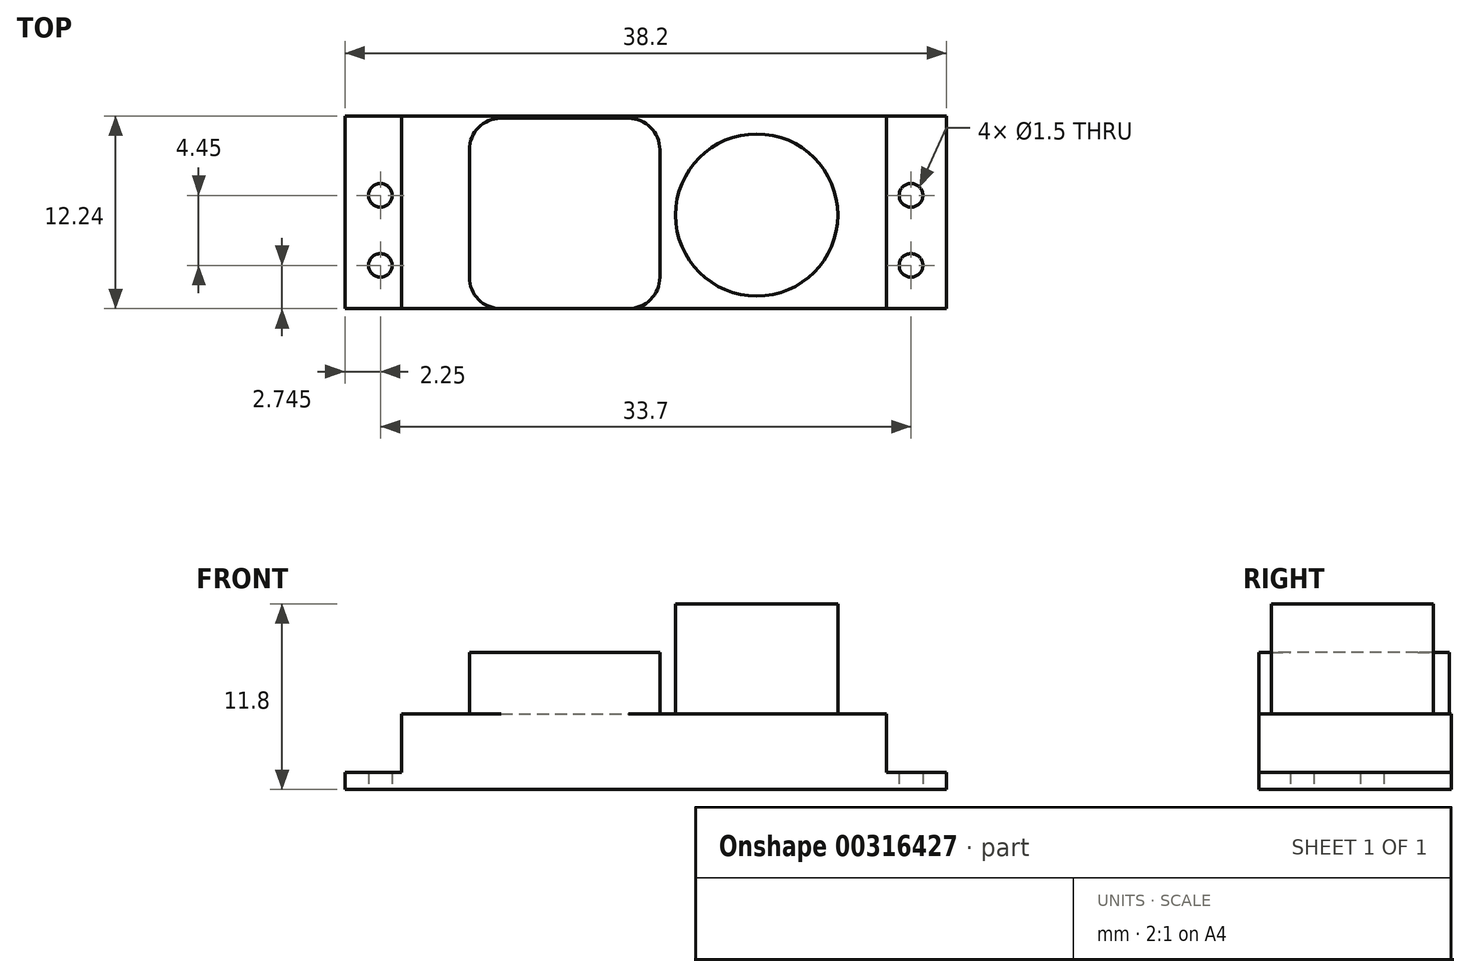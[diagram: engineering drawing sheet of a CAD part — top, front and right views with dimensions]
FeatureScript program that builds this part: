
annotation { "Feature Type Name" : "Feature", "Feature Type Description" : "" }
export const myFeature = defineFeature(function(context is Context, id is Id, definition is map)
    precondition{}
    {
        {
            var Q0;
            Q0=qCreatedBy(makeId("Top.planeOp"),FACE);
            var sketch = newSketch(context, id + "F0", { "sketchPlane" : qUnion([Q0])});
            skLineSegment(sketch, "E0.bottom", {"start": v(-19.1, 6.12) * mm, "end": v(19.1, 6.12) * mm});
            skLineSegment(sketch, "E0.top", {"start": v(-19.1, -6.12) * mm, "end": v(19.1, -6.12) * mm});
            skLineSegment(sketch, "E0.left", {"start": v(-19.1, 6.12) * mm, "end": v(-19.1, -6.12) * mm});
            skLineSegment(sketch, "E0.right", {"start": v(19.1, 6.12) * mm, "end": v(19.1, -6.12) * mm});
            skPoint(sketch, "E0.middle", {"position": v(0, 0) * mm});
            skCircle(sketch, "E1", {"center": v(-16.85, 1.08) * mm, "radius": 0.75 * mm});
            skCircle(sketch, "E2", {"center": v(-16.85, -3.38) * mm, "radius": 0.75 * mm});
            skCircle(sketch, "E3", {"center": v(16.85, 1.08) * mm, "radius": 0.75 * mm});
            skCircle(sketch, "E4", {"center": v(16.85, -3.38) * mm, "radius": 0.75 * mm});
            skSolve(sketch);
        }
        {
            var Q0;
            Q0 = qSketchRegion(id + "F0", true);
            extrude(context, id + "F1", {"entities" : qUnion([Q0]), "depth" : 1.1 * mm});
        }
        {
            var Q0;
            Q0=makeQuery(id+"F1.opExtrude","CAP_FACE",FACE,{"disambiguationData":[OSD([sQuery(id+"F0.wireOp",EDGE,"E0.bottom"),sQuery(id+"F0.wireOp",EDGE,"E0.top"),sQuery(id+"F0.wireOp",EDGE,"E0.left"),sQuery(id+"F0.wireOp",EDGE,"E0.right"),sQuery(id+"F0.wireOp",EDGE,"E1"),sQuery(id+"F0.wireOp",EDGE,"E2"),sQuery(id+"F0.wireOp",EDGE,"E3"),sQuery(id+"F0.wireOp",EDGE,"E4")])],"isStart":false});
            var sketch = newSketch(context, id + "F2", { "sketchPlane" : qUnion([Q0])});
            skLineSegment(sketch, "E5", {"start": v(-15.5, 6.12) * mm, "end": v(-15.5, -6.12) * mm});
            skLineSegment(sketch, "E6", {"start": v(15.3, 6.12) * mm, "end": v(15.3, -6.12) * mm});
            skSolve(sketch);
        }
        {
            var Q0;
            {var subQ0=sQuery(id+"F2.wireOp",EDGE,"E5");Q0=makeQuery(id+"F2.imprint","IMPRINT",FACE,{"disambiguationData":[TD([[makeQuery(id+"F2.imprint","IMPRINT",EDGE,{"derivedFrom":subQ0}),1.0]])]});}
            extrude(context, id + "F3", {"entities" : qUnion([Q0]), "operationType" : NewBodyOperationType.ADD, "depth" : 3.7 * mm});
        }
        {
            var Q0;
            Q0=makeQuery(id+"F3.opExtrude","CAP_FACE",FACE,{"disambiguationData":[OSD([sQuery(id+"F0.wireOp",EDGE,"E0.bottom"),sQuery(id+"F0.wireOp",EDGE,"E0.top"),sQuery(id+"F2.wireOp",EDGE,"E5"),sQuery(id+"F2.wireOp",EDGE,"E6")])],"isStart":false});
            var sketch = newSketch(context, id + "F4", { "sketchPlane" : qUnion([Q0])});
            skLineSegment(sketch, "E7.bottom", {"start": v(-9.2, 5.97) * mm, "end": v(-1.1, 5.97) * mm});
            skLineSegment(sketch, "E7.top", {"start": v(-9.2, -6.12) * mm, "end": v(-1.1, -6.12) * mm});
            skLineSegment(sketch, "E7.left", {"start": v(-11.2, 3.97) * mm, "end": v(-11.2, -4.12) * mm});
            skLineSegment(sketch, "E7.right", {"start": v(0.9, 3.97) * mm, "end": v(0.9, -4.12) * mm});
            skCircle(sketch, "E8", {"center": v(7.05, -0.17) * mm, "radius": 5.15 * mm});
            skPoint(sketch, "E9.visualSharp", {"position": v(-11.2, 5.97) * mm});
            skArc(sketch, "E9.filletArc", {"start": v(-9.2, 5.97) * mm, "mid": v(-10.61, 5.39) * mm, "end": v(-11.2, 3.97) * mm});
            skPoint(sketch, "E10.visualSharp", {"position": v(0.9, 5.97) * mm});
            skArc(sketch, "E10.filletArc", {"start": v(0.9, 3.97) * mm, "mid": v(0.31, 5.39) * mm, "end": v(-1.1, 5.97) * mm});
            skPoint(sketch, "E11.visualSharp", {"position": v(0.9, -6.12) * mm});
            skArc(sketch, "E11.filletArc", {"start": v(-1.1, -6.12) * mm, "mid": v(0.31, -5.54) * mm, "end": v(0.9, -4.12) * mm});
            skPoint(sketch, "E12.visualSharp", {"position": v(-11.2, -6.12) * mm});
            skArc(sketch, "E12.filletArc", {"start": v(-11.2, -4.12) * mm, "mid": v(-10.61, -5.54) * mm, "end": v(-9.2, -6.12) * mm});
            skSolve(sketch);
        }
        {
            var Q0;
            Q0=makeQuery(id+"F4.imprint","IMPRINT",FACE,{"disambiguationData":[TD([[makeQuery(id+"F4.imprint","IMPRINT",EDGE,{"derivedFrom":sQuery(id+"F4.wireOp",EDGE,"E7.bottom")}),-1.0]])]});
            extrude(context, id + "F5", {"entities" : qUnion([Q0]), "operationType" : NewBodyOperationType.ADD, "depth" : 3.9 * mm});
        }
        {
            var Q0;
            Q0=makeQuery(id+"F4.imprint","IMPRINT",FACE,{"disambiguationData":[TD([[makeQuery(id+"F4.imprint","IMPRINT",EDGE,{"derivedFrom":sQuery(id+"F4.wireOp",EDGE,"E8")}),1.0]])]});
            extrude(context, id + "F6", {"entities" : qUnion([Q0]), "operationType" : NewBodyOperationType.ADD, "depth" : 7 * mm});
        }
    });
